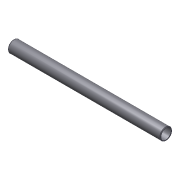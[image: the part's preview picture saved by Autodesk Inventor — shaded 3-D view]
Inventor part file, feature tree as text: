
AUTODESK INVENTOR PART (.ipt)
format: ipt  version: 2012 (Build 160160000, 160)  size: 108,544 bytes
history: native  units: in
note: dims shown in document units (in); Inventor stores cm internally (conversion verified against a paired STEP export)
features: other x42, revolve x1, sketch x1
ambient origin geometry x8: Origin, YZ Plane, XZ Plane, XY Plane, X Axis, Y Axis, Z Axis, Center Point
bodies: Solid1 (feature_tree)
feature tree (44):
  revolve  "Revolution1"  [1 undecoded]
  other  "tube_front_XY"
  other  "tube_front_YZ"
  other  "tube_front_ZX"
  other  "tube_front_X"
  other  "tube_front_Y"
  other  "tube_front_Z"
  other  "tube_front_Center"
  other  "tube_rear_XY"
  other  "tube_rear_YZ"
  other  "tube_rear_ZX"
  other  "tube_rear_X"
  other  "tube_rear_Y"
  other  "tube_rear_Z"
  other  "tube_rear_Center"
  other  "cp1_XY"
  other  "cp1_YZ"
  other  "cp1_ZX"
  other  "cp1_X"
  other  "cp1_Y"
  other  "cp1_Z"
  other  "cp1_Center"
  other  "cp2_XY"
  other  "cp2_YZ"
  other  "cp2_ZX"
  other  "cp2_X"
  other  "cp2_Y"
  other  "cp2_Z"
  other  "cp2_Center"
  other  "cp3_XY"
  other  "cp3_YZ"
  other  "cp3_ZX"
  other  "cp3_X"
  other  "cp3_Y"
  other  "cp3_Z"
  other  "cp3_Center"
  other  "cp4_XY"
  other  "cp4_YZ"
  other  "cp4_ZX"
  other  "cp4_X"
  other  "cp4_Y"
  other  "cp4_Z"
  other  "cp4_Center"
  sketch  "Sketch_1"  dims[d0=360.0deg]
note: 1 required parameter value undecoded (feature->parameter linkage not recoverable at this tier; creation-order binding heuristic only, values carry confidence <= 0.55)
